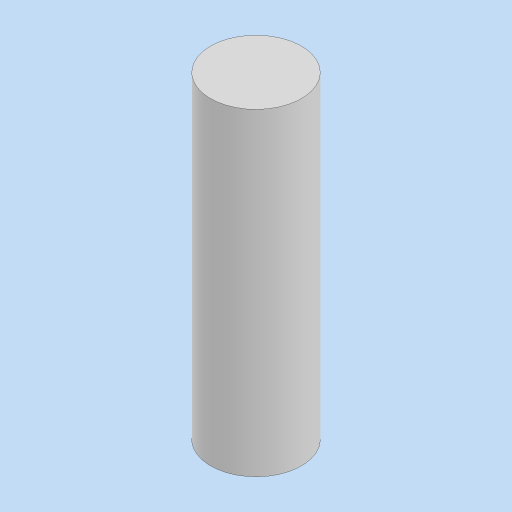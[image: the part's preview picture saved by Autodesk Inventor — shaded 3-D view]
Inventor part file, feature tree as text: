
AUTODESK INVENTOR PART (.ipt)
format: ipt  version: 2024 (Build 280153000, 153)  size: 80,896 bytes
history: native  units: in
note: dims shown in document units (in); Inventor stores cm internally (conversion verified against a paired STEP export)
features: extrude x1, sketch x1
ambient origin geometry x8: Origin, YZ Plane, XZ Plane, XY Plane, X Axis, Y Axis, Z Axis, Center Point
bodies: Solid1 (feature_tree)
feature tree (2):
  extrude  "Extrusion1"  Depth=1.75in TaperAngle=0.0deg
  sketch  "Sketch1"  dims[d0=0.5in d1=1.75in d2=0.0in]
